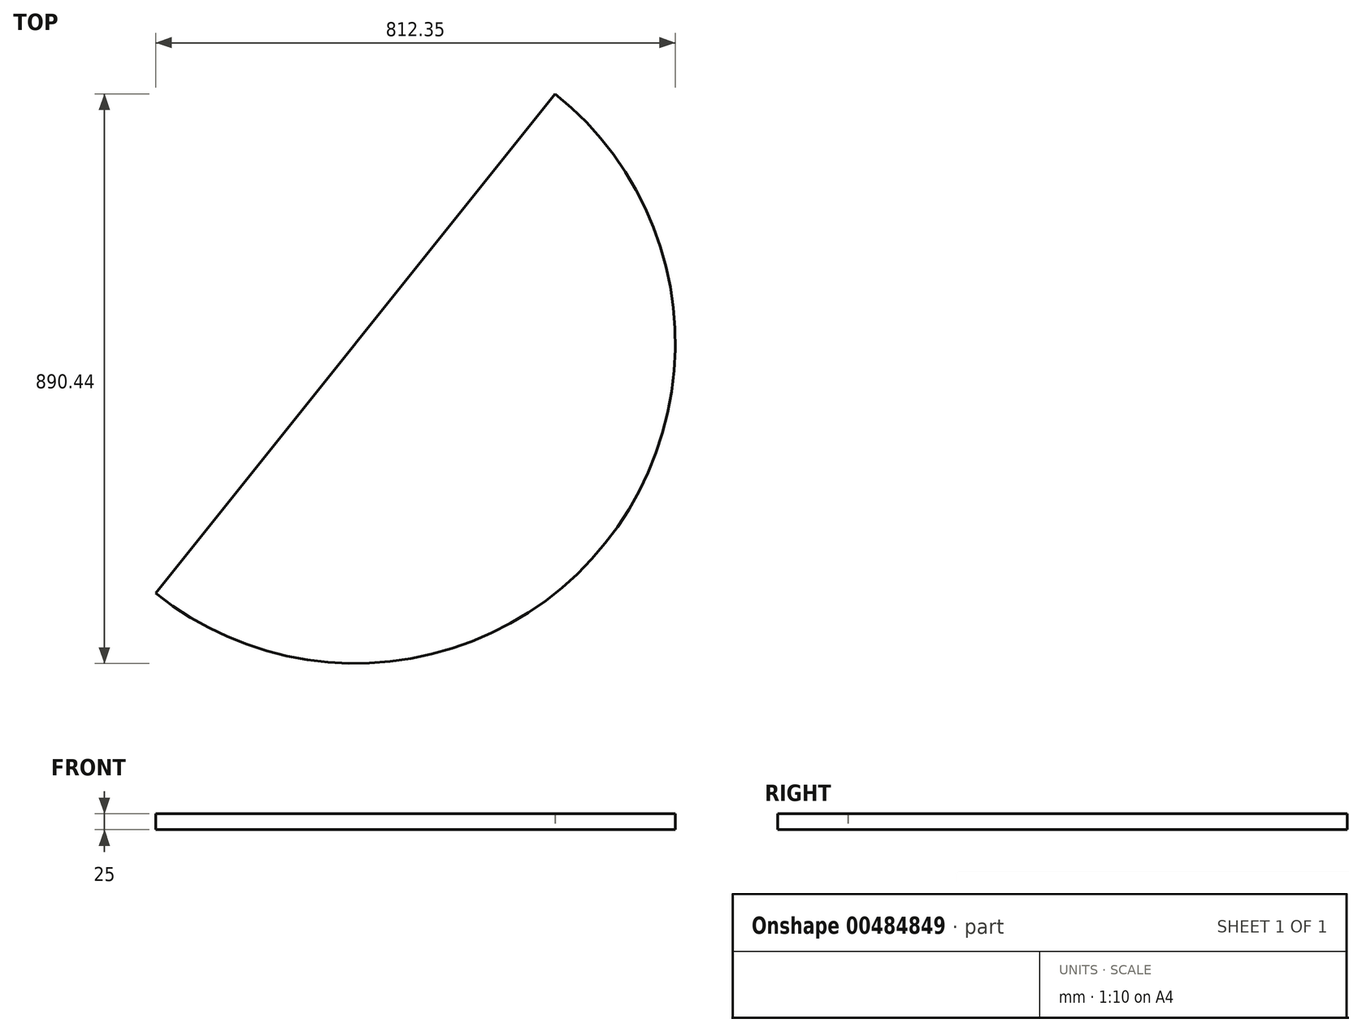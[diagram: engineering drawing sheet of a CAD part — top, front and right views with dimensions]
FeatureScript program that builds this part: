
annotation { "Feature Type Name" : "Feature", "Feature Type Description" : "" }
export const myFeature = defineFeature(function(context is Context, id is Id, definition is map)
    precondition{}
    {
        {
            var Q0;
            Q0=qCreatedBy(makeId("Top.planeOp"),FACE);
            var sketch = newSketch(context, id + "F0", { "sketchPlane" : qUnion([Q0])});
            skArc(sketch, "E0", {"start": v(-493.72, -309.34) * mm, "mid": v(209.07, -231.26) * mm, "end": v(130.98, 471.53) * mm});
            skLineSegment(sketch, "E1", {"start": v(130.98, 471.53) * mm, "end": v(-493.72, -309.34) * mm});
            skSolve(sketch);
        }
        {
            var Q0;
            Q0 = qSketchRegion(id + "F0", true);
            extrude(context, id + "F1", {"entities" : qUnion([Q0]), "depth" : 25 * mm});
        }
    });
